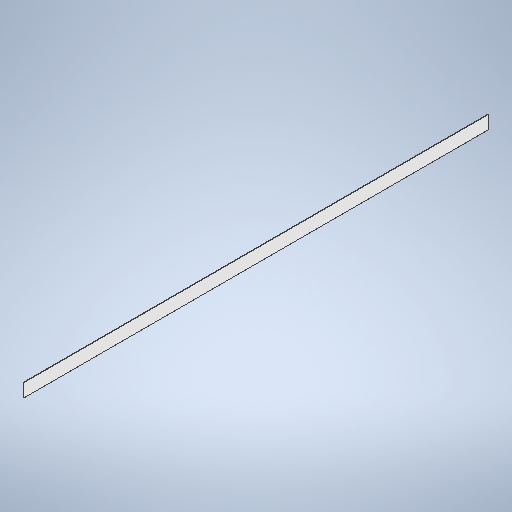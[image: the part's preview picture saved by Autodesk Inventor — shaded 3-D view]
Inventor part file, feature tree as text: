
AUTODESK INVENTOR PART (.ipt)
format: ipt  version: 2025 (Build 290162010, 162A)  size: 248,320 bytes
history: native  units: in
note: dims shown in document units (in); Inventor stores cm internally (conversion verified against a paired STEP export)
features: extrude x1, sketch x1
ambient origin geometry x8: Origin, YZ Plane, XZ Plane, XY Plane, X Axis, Y Axis, Z Axis, Center Point
bodies: Solid1 (feature_tree)
feature tree (2):
  extrude  "Extrusion1"  Depth=0.3125in TaperAngle=0.0deg
  sketch  "Sketch1"  dims[d1=8.25in d2=0.3125in d3=0.0in d4=289.0in]
